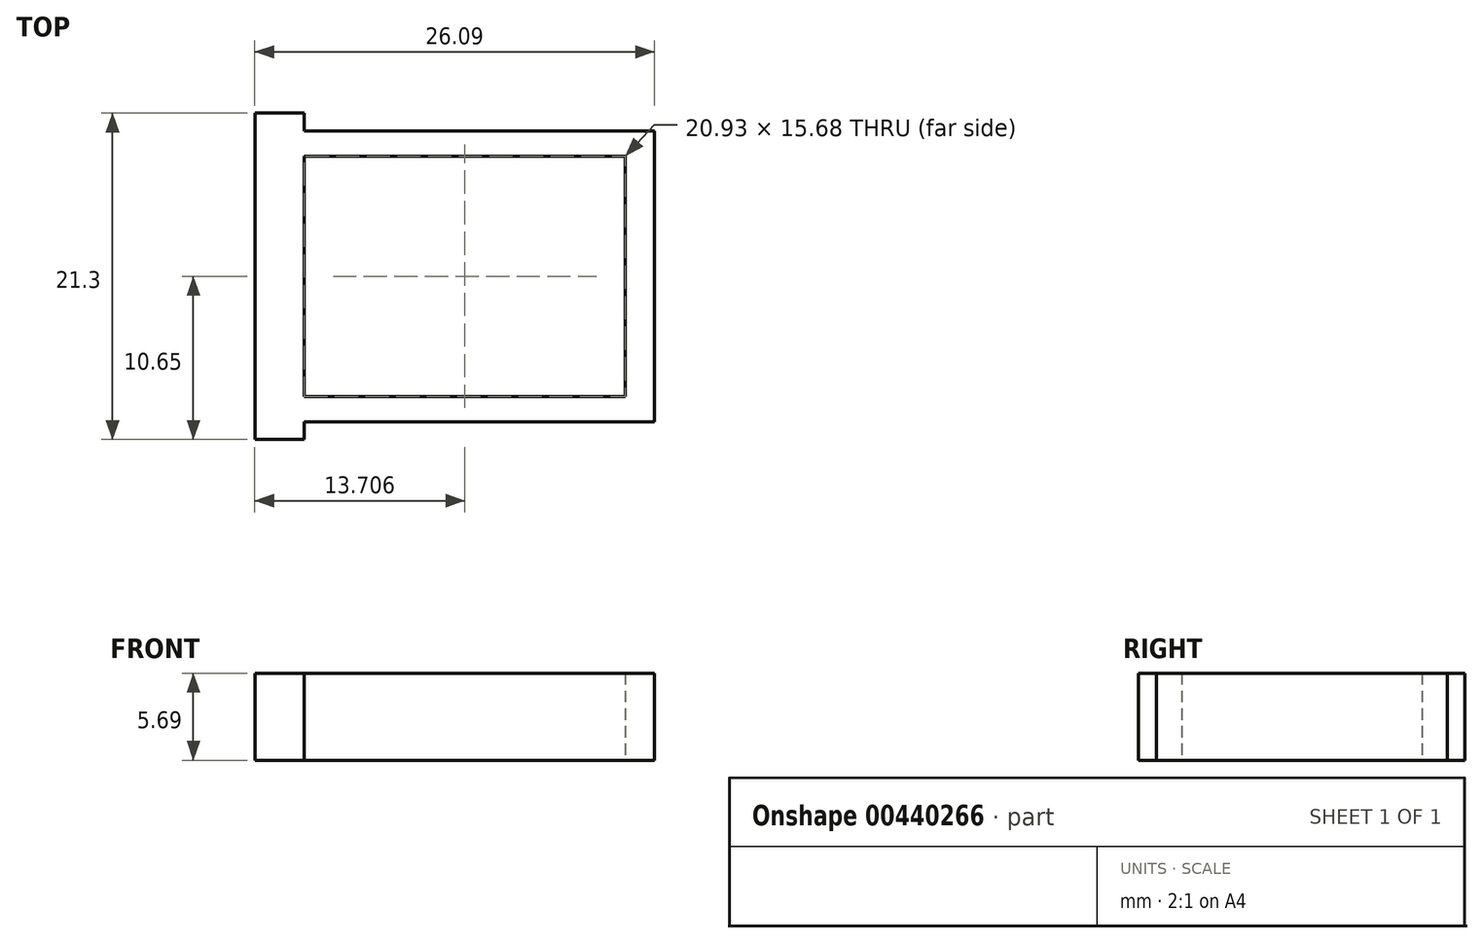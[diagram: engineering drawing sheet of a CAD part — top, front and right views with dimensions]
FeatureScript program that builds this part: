
annotation { "Feature Type Name" : "Feature", "Feature Type Description" : "" }
export const myFeature = defineFeature(function(context is Context, id is Id, definition is map)
    precondition{}
    {
        {
            var Q0;
            Q0=qCreatedBy(makeId("Top.planeOp"),FACE);
            var sketch = newSketch(context, id + "F0", { "sketchPlane" : qUnion([Q0])});
            skLineSegment(sketch, "E0.bottom", {"start": v(11.43, -9.49) * mm, "end": v(-11.43, -9.49) * mm});
            skLineSegment(sketch, "E0.top", {"start": v(11.43, 9.49) * mm, "end": v(-11.43, 9.49) * mm});
            skLineSegment(sketch, "E0.left", {"start": v(11.43, -9.49) * mm, "end": v(11.43, 9.49) * mm});
            skPoint(sketch, "E0.middle", {"position": v(0, 0) * mm});
            skLineSegment(sketch, "E1.right", {"start": v(-14.66, 9.49) * mm, "end": v(-14.66, -9.46) * mm});
            skLineSegment(sketch, "E2.top", {"start": v(-14.66, 10.65) * mm, "end": v(-11.43, 10.65) * mm});
            skLineSegment(sketch, "E2.left", {"start": v(-14.66, 9.49) * mm, "end": v(-14.66, 10.65) * mm});
            skLineSegment(sketch, "E2.right", {"start": v(-11.43, 9.49) * mm, "end": v(-11.43, 10.65) * mm});
            skLineSegment(sketch, "E3.MirrorCS", {"start": v(-14.66, -9.49) * mm, "end": v(-14.66, -10.65) * mm});
            skLineSegment(sketch, "E4.MirrorCS", {"start": v(-14.66, -10.65) * mm, "end": v(-11.43, -10.65) * mm});
            skLineSegment(sketch, "E5.MirrorCS", {"start": v(-11.43, -9.49) * mm, "end": v(-11.43, -10.65) * mm});
            skLineSegment(sketch, "E6.bottom", {"start": v(9.51, -7.84) * mm, "end": v(-11.42, -7.84) * mm});
            skLineSegment(sketch, "E6.top", {"start": v(9.51, 7.84) * mm, "end": v(-11.42, 7.84) * mm});
            skLineSegment(sketch, "E6.left", {"start": v(9.51, -7.84) * mm, "end": v(9.51, 7.84) * mm});
            skLineSegment(sketch, "E6.right", {"start": v(-11.42, -7.84) * mm, "end": v(-11.42, 7.84) * mm});
            skPoint(sketch, "E6.middle", {"position": v(-0.95, 0) * mm});
            skLineSegment(sketch, "E7", {"start": v(-14.66, 10.65) * mm, "end": v(-14.66, -10.65) * mm});
            skSolve(sketch);
        }
        {
            var Q0;
            Q0=makeQuery(id+"F0.imprint","IMPRINT",FACE,{"disambiguationData":[TD([[makeQuery(id+"F0.imprint","IMPRINT",EDGE,{"derivedFrom":sQuery(id+"F0.wireOp",EDGE,"E0.bottom")}),-1.0]])]});
            extrude(context, id + "F1", {"entities" : qUnion([Q0]), "depth" : 5.7 * mm});
        }
    });
